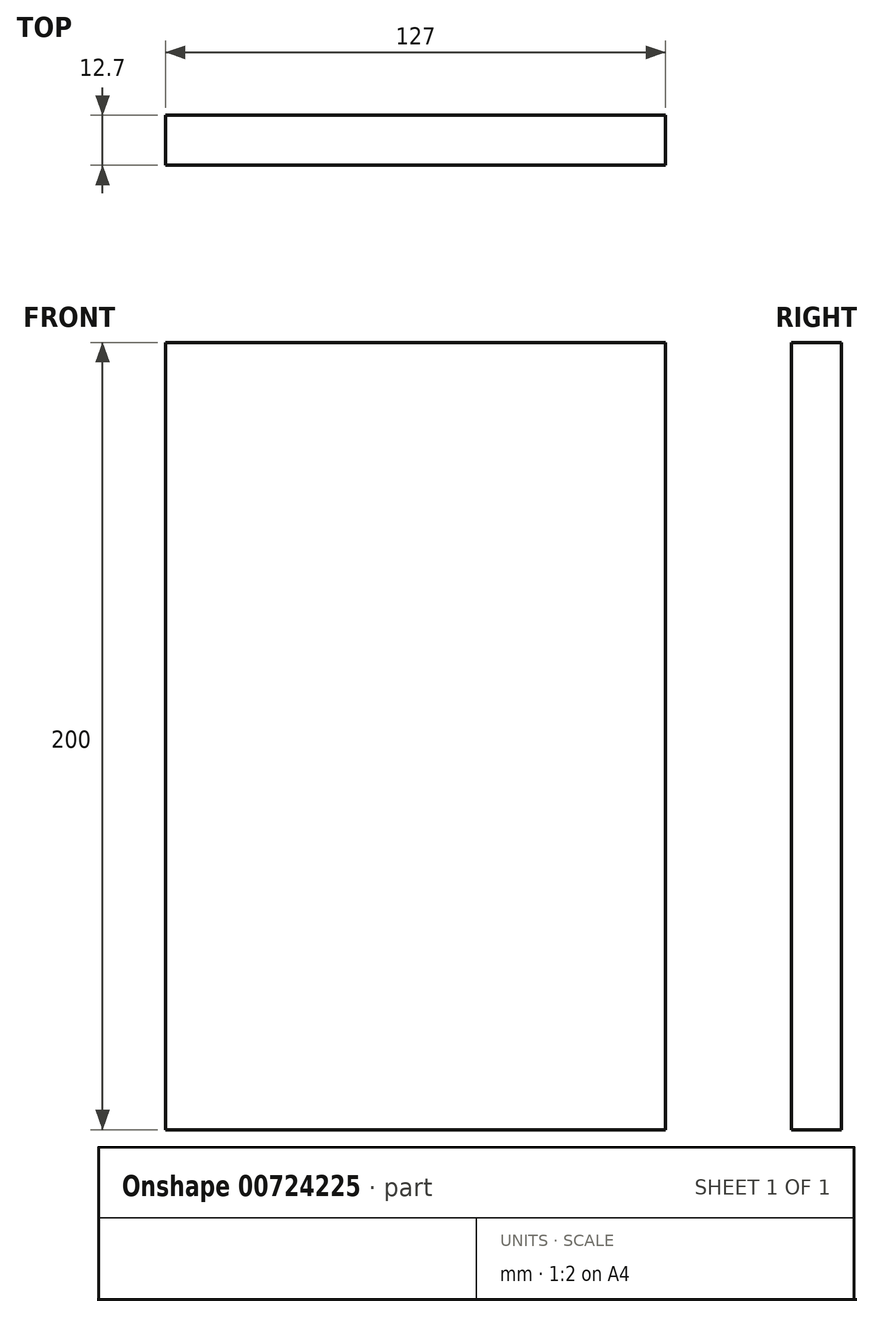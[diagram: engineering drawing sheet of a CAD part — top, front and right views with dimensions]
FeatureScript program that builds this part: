
annotation { "Feature Type Name" : "Feature", "Feature Type Description" : "" }
export const myFeature = defineFeature(function(context is Context, id is Id, definition is map)
    precondition{}
    {
        {
            var Q0;
            Q0=qCreatedBy(makeId("Front.planeOp"),FACE);
            var sketch = newSketch(context, id + "F0", { "sketchPlane" : qUnion([Q0])});
            skLineSegment(sketch, "E0.bottom", {"start": v(-64.53, 140.87) * mm, "end": v(62.47, 140.87) * mm});
            skLineSegment(sketch, "E0.top", {"start": v(-64.53, -59.13) * mm, "end": v(62.47, -59.13) * mm});
            skLineSegment(sketch, "E0.left", {"start": v(-64.53, 140.87) * mm, "end": v(-64.53, -59.13) * mm});
            skLineSegment(sketch, "E0.right", {"start": v(62.47, 140.87) * mm, "end": v(62.47, -59.13) * mm});
            skSolve(sketch);
        }
        {
            var Q0;
            Q0 = qSketchRegion(id + "F0", true);
            extrude(context, id + "F1", {"entities" : qUnion([Q0]), "depth" : 12.7 * mm, "offsetDistance" : 25.4 * mm});
        }
    });
